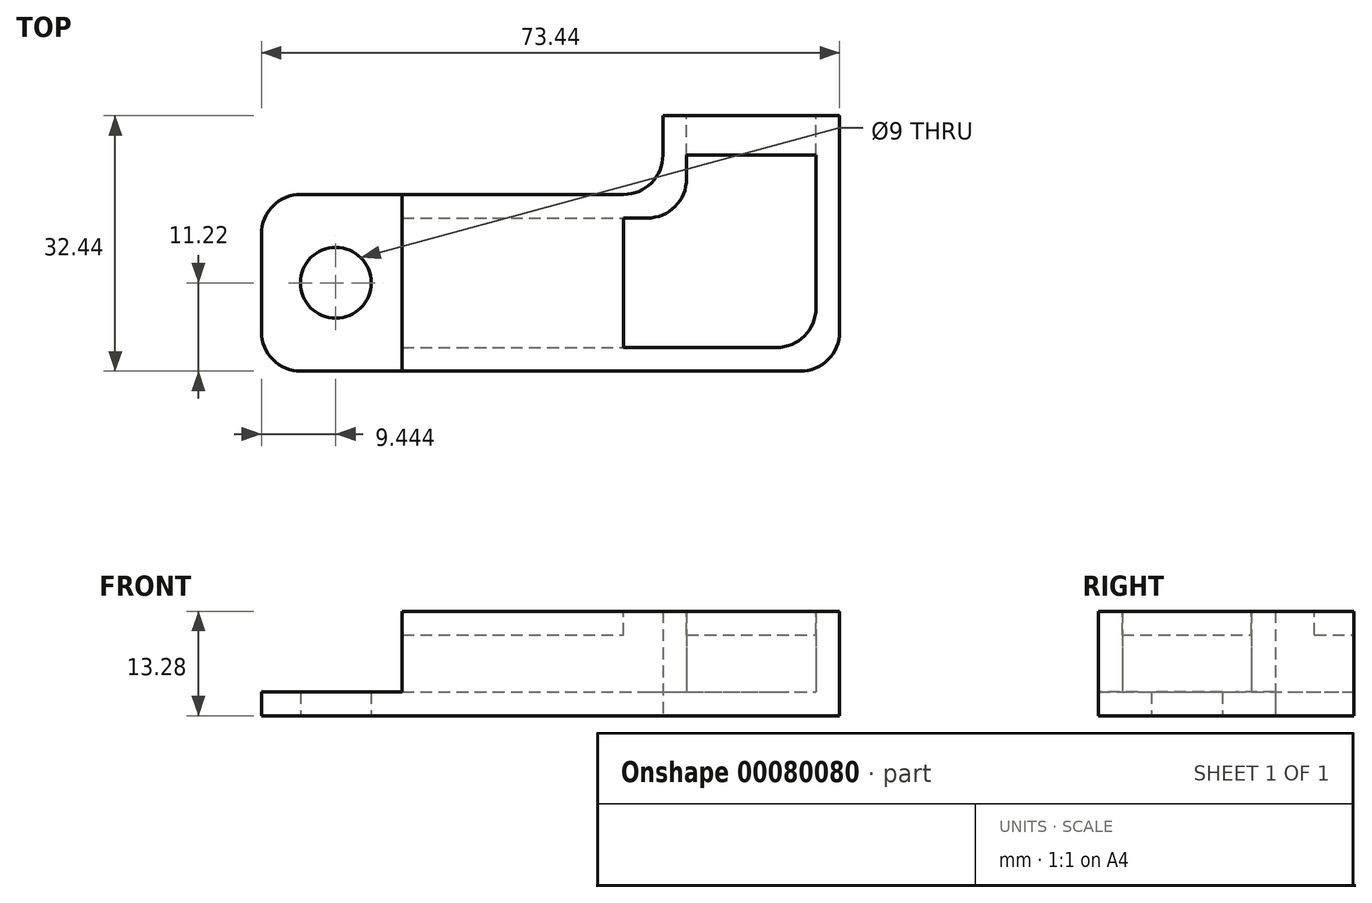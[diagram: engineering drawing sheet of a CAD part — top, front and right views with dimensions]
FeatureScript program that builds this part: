
annotation { "Feature Type Name" : "Feature", "Feature Type Description" : "" }
export const myFeature = defineFeature(function(context is Context, id is Id, definition is map)
    precondition{}
    {
        {
            var Q0;
            Q0=qCreatedBy(makeId("Top.planeOp"),FACE);
            var sketch = newSketch(context, id + "F0", { "sketchPlane" : qUnion([Q0])});
            skLineSegment(sketch, "E0.bottom", {"start": v(-20.32, 0) * mm, "end": v(30.68, 0) * mm});
            skLineSegment(sketch, "E0.top", {"start": v(-20.32, 22.44) * mm, "end": v(30.68, 22.44) * mm});
            skLineSegment(sketch, "E0.left", {"start": v(-20.32, 0) * mm, "end": v(-20.32, 22.44) * mm});
            skLineSegment(sketch, "E0.right", {"start": v(30.68, 0) * mm, "end": v(30.68, 22.44) * mm});
            skLineSegment(sketch, "E1.bottom", {"start": v(30.68, 0) * mm, "end": v(53.12, 0) * mm});
            skLineSegment(sketch, "E1.top", {"start": v(30.68, 32.44) * mm, "end": v(53.12, 32.44) * mm});
            skLineSegment(sketch, "E1.left", {"start": v(30.68, 0) * mm, "end": v(30.68, 32.44) * mm});
            skLineSegment(sketch, "E1.right", {"start": v(53.12, 0) * mm, "end": v(53.12, 32.44) * mm});
            skCircle(sketch, "E2", {"center": v(-10.88, 11.22) * mm, "radius": 4.5 * mm});
            skPoint(sketch, "E3", {"position": v(-20.32, 11.22) * mm});
            skLineSegment(sketch, "E4", {"start": v(-2.44, 0) * mm, "end": v(-2.44, 22.44) * mm});
            skSolve(sketch);
        }
        {
            var Q0;
            {var subQ3=sQuery(id+"F0.wireOp",EDGE,"E1.bottom");Q0=makeQuery(id+"F0.imprint","IMPRINT",FACE,{"disambiguationData":[TD([[makeQuery(id+"F0.imprint","IMPRINT",EDGE,{"derivedFrom":subQ3}),1.0]])]});}
            var Q1;
            {var subQ3=sQuery(id+"F0.wireOp",EDGE,"E4");Q1=makeQuery(id+"F0.imprint","IMPRINT",FACE,{"disambiguationData":[TD([[makeQuery(id+"F0.imprint","IMPRINT",EDGE,{"derivedFrom":subQ3}),-1.0]])]});}
            extrude(context, id + "F1", {"entities" : qUnion([Q0, Q1]), "depth" : 13.28 * mm});
        }
        {
            var Q0;
            {var subQ0=sQuery(id+"F0.wireOp",EDGE,"E0.left");Q0=makeQuery(id+"F0.imprint","IMPRINT",FACE,{"disambiguationData":[TD([[makeQuery(id+"F0.imprint","IMPRINT",EDGE,{"derivedFrom":subQ0}),-1.0]])]});}
            extrude(context, id + "F2", {"entities" : qUnion([Q0]), "operationType" : NewBodyOperationType.ADD, "depth" : 3 * mm});
        }
        {
            var Q0;
            Q0=makeQuery(id+"F1.opExtrude","SWEPT_FACE",FACE,{"disambiguationData":[OSD([sQuery(id+"F0.wireOp",EDGE,"E4")])]});
            var Q1;
            Q1=makeQuery(id+"F1.opExtrude","SWEPT_FACE",FACE,{"disambiguationData":[OSD([sQuery(id+"F0.wireOp",EDGE,"E1.top")])]});
            shell(context, id + "F3", {"entities" : qUnion([Q0, Q1]), "thickness" : 3 * mm});
        }
        {
            var Q0;
            Q0=makeQuery(id+"F1.opExtrude","CAP_FACE",FACE,{"disambiguationData":[OSD([sQuery(id+"F0.wireOp",EDGE,"E0.bottom"),sQuery(id+"F0.wireOp",EDGE,"E0.top"),sQuery(id+"F0.wireOp",EDGE,"E1.bottom"),sQuery(id+"F0.wireOp",EDGE,"E1.top"),sQuery(id+"F0.wireOp",EDGE,"E1.left"),sQuery(id+"F0.wireOp",EDGE,"E1.right"),sQuery(id+"F0.wireOp",EDGE,"E4")])],"isStart":false});
            var sketch = newSketch(context, id + "F4", { "sketchPlane" : qUnion([Q0])});
            skLineSegment(sketch, "E5.bottom", {"start": v(33.68, 27.44) * mm, "end": v(50.12, 27.44) * mm});
            skLineSegment(sketch, "E5.top", {"start": v(33.68, 3) * mm, "end": v(50.12, 3) * mm});
            skLineSegment(sketch, "E5.left", {"start": v(33.68, 27.44) * mm, "end": v(33.68, 3) * mm});
            skLineSegment(sketch, "E5.right", {"start": v(50.12, 27.44) * mm, "end": v(50.12, 3) * mm});
            skLineSegment(sketch, "E6.bottom", {"start": v(33.68, 3) * mm, "end": v(25.68, 3) * mm});
            skLineSegment(sketch, "E6.top", {"start": v(33.68, 19.44) * mm, "end": v(25.68, 19.44) * mm});
            skLineSegment(sketch, "E6.left", {"start": v(33.68, 3) * mm, "end": v(33.68, 19.44) * mm});
            skLineSegment(sketch, "E6.right", {"start": v(25.68, 3) * mm, "end": v(25.68, 19.44) * mm});
            skLineSegment(sketch, "E7", {"start": v(29.68, 19.44) * mm, "end": v(29.68, 22.44) * mm, "construction": true});
            skLineSegment(sketch, "E8", {"start": v(29.84, 0) * mm, "end": v(29.84, 3) * mm, "construction": true});
            skLineSegment(sketch, "E9", {"start": v(50.12, 15.22) * mm, "end": v(53.12, 15.22) * mm, "construction": true});
            skLineSegment(sketch, "E10", {"start": v(33.68, 29.28) * mm, "end": v(30.68, 29.28) * mm});
            skSolve(sketch);
        }
        {
            var Q0;
            {var subQ3=sQuery(id+"F4.wireOp",EDGE,"P4Fd0WVG-2qBP-qYUX-DSYe-rzKMcoyvzPB7");Q0=makeQuery(id+"F4.imprint","IMPRINT",FACE,{"disambiguationData":[TD([[makeQuery(id+"F4.imprint","IMPRINT",EDGE,{"derivedFrom":subQ3}),1.0]])]});}
            var Q1;
            Q1=makeQuery(id+"F4.imprint","IMPRINT",FACE,{"disambiguationData":[TD([[makeQuery(id+"F4.imprint","IMPRINT",EDGE,{"derivedFrom":sQuery(id+"F4.wireOp",EDGE,"E6.bottom")}),-1.0]])]});
            var Q2;
            Q2=makeQuery(id+"F4.imprint","IMPRINT",FACE,{"disambiguationData":[TD([[makeQuery(id+"F4.imprint","IMPRINT",EDGE,{"derivedFrom":sQuery(id+"F4.wireOp",EDGE,"E5.bottom")}),-1.0]])]});
            extrude(context, id + "F5", {"entities" : qUnion([Q0, Q1, Q2]), "operationType" : NewBodyOperationType.REMOVE, "oppositeDirection" : true, "depth" : 3 * mm});
        }
        {
            var Q0;
            Q0=makeQuery(id+"F1.opExtrude","SWEPT_EDGE",EDGE,{"disambiguationData":[OSD([sQuery(id+"F0.wireOp",EDGE,"E1.bottom"),sQuery(id+"F0.wireOp",EDGE,"E1.right")])]});
            var Q1;
            Q1=makeQuery(id+"F1.opExtrude","SWEPT_EDGE",EDGE,{"disambiguationData":[OSD([sQuery(id+"F0.wireOp",EDGE,"E0.top"),sQuery(id+"F0.wireOp",EDGE,"E1.left")])]});
            var Q2;
            Q2=makeQuery(id+"F5.boolean.opBoolean","MERGE",EDGE,{"derivedFrom":[makeQuery(id+"F3.opShell","OFFSET_EDGE",EDGE,{"disambiguationData":[OSD([sQuery(id+"F0.wireOp",EDGE,"E0.top"),sQuery(id+"F0.wireOp",EDGE,"E1.left")])]}),makeQuery(id+"F5.opExtrude","SWEPT_EDGE",EDGE,{"disambiguationData":[OSD([sQuery(id+"F4.wireOp",EDGE,"E5.left"),sQuery(id+"F4.wireOp",EDGE,"E6.top"),sQuery(id+"F4.wireOp",EDGE,"E6.left")])]})]});
            var Q3;
            Q3=makeQuery(id+"F5.boolean.opBoolean","MERGE",EDGE,{"derivedFrom":[makeQuery(id+"F3.opShell","OFFSET_EDGE",EDGE,{"disambiguationData":[OSD([sQuery(id+"F0.wireOp",EDGE,"E1.bottom"),sQuery(id+"F0.wireOp",EDGE,"E1.right")])]}),makeQuery(id+"F5.opExtrude","SWEPT_EDGE",EDGE,{"disambiguationData":[OSD([sQuery(id+"F4.wireOp",EDGE,"E5.top"),sQuery(id+"F4.wireOp",EDGE,"E5.right")])]})]});
            var Q4;
            Q4=makeQuery(id+"F2.opExtrude","SWEPT_EDGE",EDGE,{"disambiguationData":[OSD([sQuery(id+"F0.wireOp",EDGE,"E0.top"),sQuery(id+"F0.wireOp",EDGE,"E0.left")])]});
            var Q5;
            Q5=makeQuery(id+"F2.opExtrude","SWEPT_EDGE",EDGE,{"disambiguationData":[OSD([sQuery(id+"F0.wireOp",EDGE,"E0.bottom"),sQuery(id+"F0.wireOp",EDGE,"E0.left")])]});
            fillet(context, id + "F6", {"entities" : qUnion([Q0, Q1, Q2, Q3, Q4, Q5]), "radius" : 5 * mm, "tangentPropagation" : true, "allowEdgeOverflow" : false});
        }
    });
